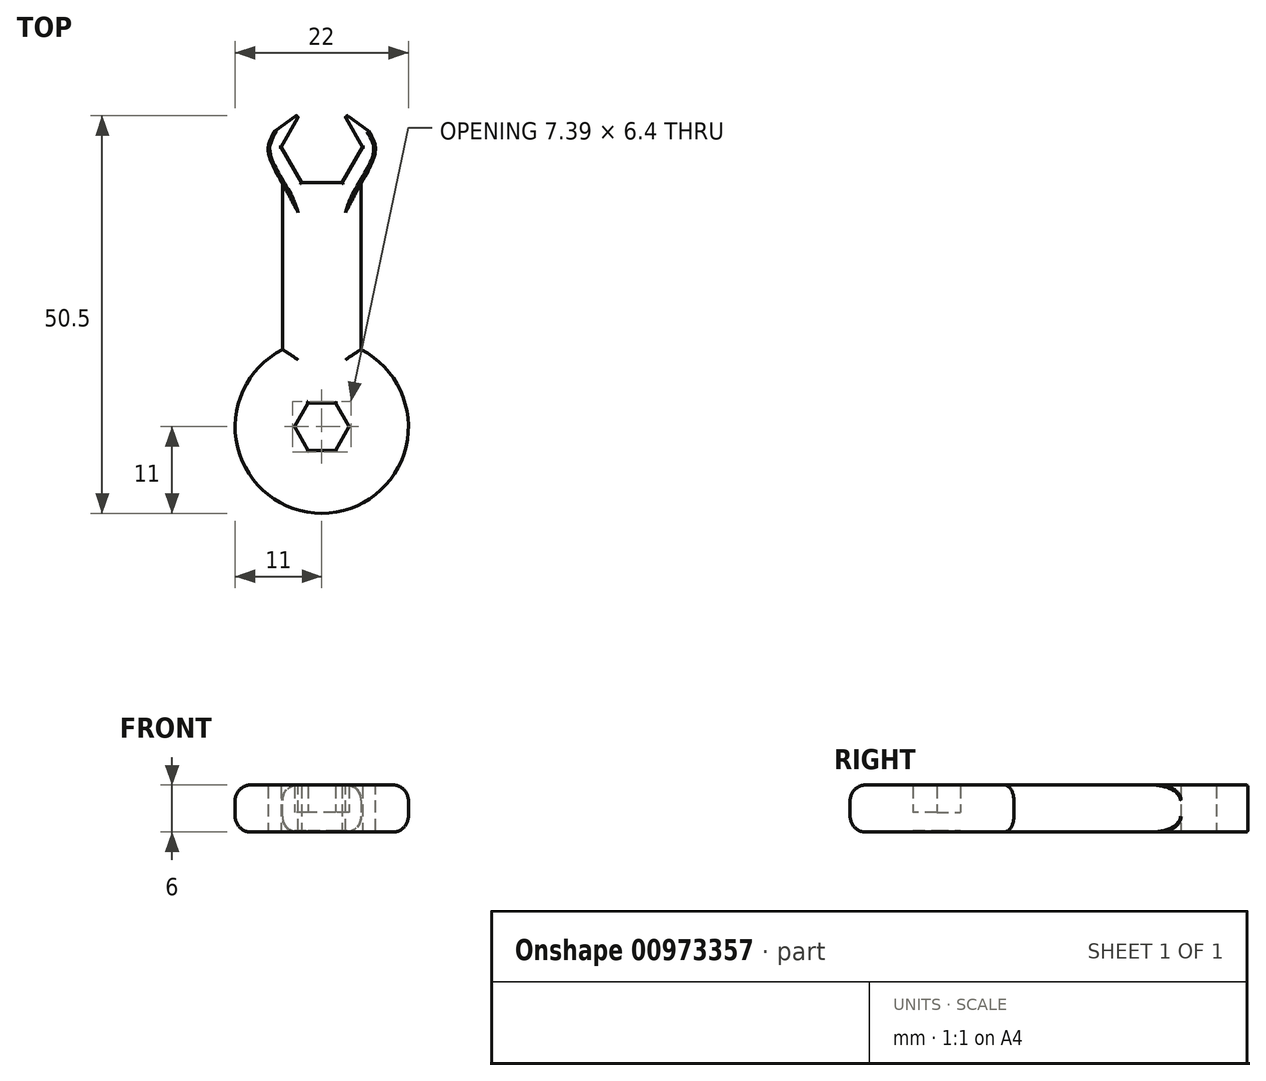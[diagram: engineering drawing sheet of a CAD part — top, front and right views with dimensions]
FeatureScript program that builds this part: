
annotation { "Feature Type Name" : "Feature", "Feature Type Description" : "" }
export const myFeature = defineFeature(function(context is Context, id is Id, definition is map)
    precondition{}
    {
        {
            var Q0;
            Q0=qCreatedBy(makeId("Top.planeOp"),FACE);
            var sketch = newSketch(context, id + "F0", { "sketchPlane" : qUnion([Q0])});
            skArc(sketch, "E0", {"start": v(-5, 9.8) * mm, "mid": v(0, -11) * mm, "end": v(5, 9.8) * mm});
            skCircle(sketch, "E1.cCircle", {"center": v(0, 0) * mm, "radius": 3 * mm, "construction": true});
            skLineSegment(sketch, "E1.0", {"start": v(1.73, -3) * mm, "end": v(-1.73, -3) * mm});
            skLineSegment(sketch, "E1.1", {"start": v(-1.73, -3) * mm, "end": v(-3.46, 0) * mm});
            skLineSegment(sketch, "E1.2", {"start": v(-3.46, 0) * mm, "end": v(-1.73, 3) * mm});
            skLineSegment(sketch, "E1.3", {"start": v(-1.73, 3) * mm, "end": v(1.73, 3) * mm});
            skLineSegment(sketch, "E1.4", {"start": v(1.73, 3) * mm, "end": v(3.46, 0) * mm});
            skLineSegment(sketch, "E1.5", {"start": v(3.46, 0) * mm, "end": v(1.73, -3) * mm});
            skPoint(sketch, "E1.0.midPoint", {"position": v(0, -3) * mm});
            skLineSegment(sketch, "E2.top", {"start": v(5, 31) * mm, "end": v(-5, 31) * mm});
            skLineSegment(sketch, "E2.left", {"start": v(5, 11) * mm, "end": v(5, 31) * mm});
            skLineSegment(sketch, "E2.right", {"start": v(-5, 11) * mm, "end": v(-5, 31) * mm});
            skLineSegment(sketch, "E3", {"start": v(5, 11) * mm, "end": v(5, 9) * mm});
            skLineSegment(sketch, "E4", {"start": v(-5, 11) * mm, "end": v(-5, 9) * mm});
            skLineSegment(sketch, "E5", {"start": v(-5, 9) * mm, "end": v(5, 9) * mm});
            skPoint(sketch, "E2.bottom.start.orphan", {"position": v(0, 11) * mm});
            skPoint(sketch, "E6.orphan", {"position": v(-8, 31) * mm});
            skPoint(sketch, "E7.startSnap0", {"position": v(0, 31) * mm});
            skPoint(sketch, "E7.end.orphan", {"position": v(0, 31) * mm});
            skPoint(sketch, "E7.start.orphan", {"position": v(0, 35.5) * mm});
            skLineSegment(sketch, "E8", {"start": v(0, 35.5) * mm, "end": v(0, 31) * mm});
            skPoint(sketch, "E9.orphan", {"position": v(2.6, 44.5) * mm});
            skPoint(sketch, "E10.5.end.orphan", {"position": v(2.6, 35.5) * mm});
            skPoint(sketch, "E10.1.start.orphan", {"position": v(-2.6, 35.5) * mm});
            skLineSegment(sketch, "E11.0", {"start": v(2.6, 31) * mm, "end": v(-2.6, 31) * mm});
            skLineSegment(sketch, "E11.1", {"start": v(-2.6, 31) * mm, "end": v(-5.2, 35.5) * mm});
            skLineSegment(sketch, "E11.5", {"start": v(5.2, 35.5) * mm, "end": v(2.6, 31) * mm});
            skPoint(sketch, "E12.orphan", {"position": v(2.6, 40) * mm});
            skPoint(sketch, "E13.start.orphan", {"position": v(-6.8, 37.68) * mm});
            skPoint(sketch, "E14.MirrorCS.end.orphan", {"position": v(5.2, 35.5) * mm});
            skPoint(sketch, "E14.MirrorCS.start.orphan", {"position": v(6.8, 37.68) * mm});
            skPoint(sketch, "E15.MirrorCS.start.orphan", {"position": v(9.24, 35.24) * mm});
            skCircle(sketch, "E16.cCircle", {"center": v(0, 35.5) * mm, "radius": 4.5 * mm, "construction": true});
            skLineSegment(sketch, "E16.3", {"start": v(-5.2, 35.5) * mm, "end": v(-2.6, 40) * mm});
            skLineSegment(sketch, "E16.5", {"start": v(2.6, 40) * mm, "end": v(5.2, 35.5) * mm});
            skPoint(sketch, "E16.0.midPoint", {"position": v(3.9, 33.25) * mm});
            skLineSegment(sketch, "E17", {"start": v(-5.92, 37.62) * mm, "end": v(-2.6, 40) * mm});
            skLineSegment(sketch, "E18", {"start": v(2.6, 40) * mm, "end": v(5.92, 37.62) * mm});
            skPoint(sketch, "E19.orphan", {"position": v(-7.81, 37.68) * mm});
            skPoint(sketch, "E20.MirrorCS.end.orphan", {"position": v(7.81, 37.68) * mm});
            skPoint(sketch, "E21.end.orphan", {"position": v(-5.92, 37.62) * mm});
            skFitSpline(sketch, "E22", {"points": [v(-5, 31) * mm, v(-6.8, 35.24) * mm, v(-5.92, 37.62) * mm], "startDerivative": vector(-4.66, 7.9) * mm, "endDerivative": vector(3.2, 5.2) * mm});
            skPoint(sketch, "E23.orphan", {"position": v(-9.24, 35.24) * mm});
            skFitSpline(sketch, "E24.MirrorCS", {"points": [v(5, 31) * mm, v(6.8, 35.24) * mm, v(5.92, 37.62) * mm], "startDerivative": vector(4.66, 7.9) * mm, "endDerivative": vector(-3.2, 5.2) * mm});
            skSolve(sketch);
        }
        {
            var Q0;
            {var subQ1=sQuery(id+"F0.wireOp",EDGE,"E0");Q0=makeQuery(id+"F0.imprint","IMPRINT",FACE,{"disambiguationData":[TD([[makeQuery(id+"F0.imprint","IMPRINT",EDGE,{"derivedFrom":subQ1}),1.0]])]});}
            var Q1;
            {var subQ7=sQuery(id+"F0.wireOp",EDGE,"E2.left");Q1=makeQuery(id+"F0.imprint","IMPRINT",FACE,{"disambiguationData":[TD([[makeQuery(id+"F0.imprint","IMPRINT",EDGE,{"derivedFrom":subQ7}),1.0]])]});}
            var Q2;
            {var subQ0=sQuery(id+"F0.wireOp",EDGE,"E11.1");Q2=makeQuery(id+"F0.imprint","IMPRINT",FACE,{"disambiguationData":[TD([[makeQuery(id+"F0.imprint","IMPRINT",EDGE,{"derivedFrom":subQ0}),1.0]])]});}
            var Q3;
            {var subQ0=sQuery(id+"F0.wireOp",EDGE,"E11.5");Q3=makeQuery(id+"F0.imprint","IMPRINT",FACE,{"disambiguationData":[TD([[makeQuery(id+"F0.imprint","IMPRINT",EDGE,{"derivedFrom":subQ0}),1.0]])]});}
            extrude(context, id + "F1", {"entities" : qUnion([Q0, Q1, Q2, Q3]), "depth" : 6 * mm, "offsetDistance" : 25 * mm});
        }
        {
            var Q0;
            Q0=makeQuery(id+"F1.opExtrude","SWEPT_EDGE",EDGE,{"disambiguationData":[OSD([sQuery(id+"F0.wireOp",EDGE,"KDg4HD6V-isxW-cNXE-fjSG-ZOqcz2IWWXIc"),sQuery(id+"F0.wireOp",EDGE,"Dl8Gz6KM-Olm8-RAhG-Kqo9-J7DI2SJ82FjE")])]});
            var Q1;
            Q1=makeQuery(id+"F1.opExtrude","SWEPT_EDGE",EDGE,{"disambiguationData":[OSD([sQuery(id+"F0.wireOp",EDGE,"7af5c376-e6ad-482c-982b-24b6638f54230.MirrorCS"),sQuery(id+"F0.wireOp",EDGE,"E20.MirrorCS")])]});
            var Q2;
            Q2=makeQuery(id+"F1.opExtrude","CAP_EDGE",EDGE,{"disambiguationData":[OSD([sQuery(id+"F0.wireOp",EDGE,"E2.left"),sQuery(id+"F0.wireOp",EDGE,"E3")])],"isStart":false});
            var Q3;
            Q3=makeQuery(id+"F1.opExtrude","CAP_EDGE",EDGE,{"disambiguationData":[OSD([sQuery(id+"F0.wireOp",EDGE,"E2.right"),sQuery(id+"F0.wireOp",EDGE,"E4")])],"isStart":false});
            var Q4;
            Q4=makeQuery(id+"F1.opExtrude","CAP_EDGE",EDGE,{"disambiguationData":[OSD([sQuery(id+"F0.wireOp",EDGE,"E2.right"),sQuery(id+"F0.wireOp",EDGE,"E4")])],"isStart":true});
            var Q5;
            Q5=makeQuery(id+"F1.opExtrude","CAP_EDGE",EDGE,{"disambiguationData":[OSD([sQuery(id+"F0.wireOp",EDGE,"E2.left"),sQuery(id+"F0.wireOp",EDGE,"E3")])],"isStart":true});
            var Q6;
            Q6=makeQuery(id+"F1.opExtrude","CAP_EDGE",EDGE,{"disambiguationData":[OSD([sQuery(id+"F0.wireOp",EDGE,"E0")])],"isStart":true});
            var Q7;
            Q7=makeQuery(id+"F1.opExtrude","CAP_EDGE",EDGE,{"disambiguationData":[OSD([sQuery(id+"F0.wireOp",EDGE,"E0")])],"isStart":false});
            fillet(context, id + "F2", {"entities" : qUnion([Q0, Q1, Q2, Q3, Q4, Q5, Q6, Q7]), "tangentPropagation" : true, "radius" : 2 * mm, "defaultsChanged" : false, "vertexSettings" : [], "allowEdgeOverflow" : false});
        }
        {
            var Q0;
            Q0=makeQuery(id+"F1.opExtrude","SWEPT_FACE",FACE,{"disambiguationData":[OSD([sQuery(id+"F0.wireOp",EDGE,"E18")])]});
            var Q1;
            Q1=makeQuery(id+"F1.opExtrude","SWEPT_FACE",FACE,{"disambiguationData":[OSD([sQuery(id+"F0.wireOp",EDGE,"E24.MirrorCS")])]});
            var Q2;
            Q2=makeQuery(id+"F1.opExtrude","CAP_FACE",FACE,{"disambiguationData":[OSD([sQuery(id+"F0.wireOp",EDGE,"E0"),sQuery(id+"F0.wireOp",EDGE,"E1.0"),sQuery(id+"F0.wireOp",EDGE,"E1.1"),sQuery(id+"F0.wireOp",EDGE,"E1.2"),sQuery(id+"F0.wireOp",EDGE,"E1.3"),sQuery(id+"F0.wireOp",EDGE,"E1.4"),sQuery(id+"F0.wireOp",EDGE,"E1.5"),sQuery(id+"F0.wireOp",EDGE,"E2.top"),sQuery(id+"F0.wireOp",EDGE,"E2.left"),sQuery(id+"F0.wireOp",EDGE,"E2.right"),sQuery(id+"F0.wireOp",EDGE,"E3"),sQuery(id+"F0.wireOp",EDGE,"E4"),sQuery(id+"F0.wireOp",EDGE,"E11.1"),sQuery(id+"F0.wireOp",EDGE,"E11.5"),sQuery(id+"F0.wireOp",EDGE,"E16.3"),sQuery(id+"F0.wireOp",EDGE,"E16.5"),sQuery(id+"F0.wireOp",EDGE,"E17"),sQuery(id+"F0.wireOp",EDGE,"E18"),sQuery(id+"F0.wireOp",EDGE,"E22"),sQuery(id+"F0.wireOp",EDGE,"E24.MirrorCS")])],"isStart":true});
            var Q3;
            Q3=makeQuery(id+"F1.opExtrude","SWEPT_FACE",FACE,{"disambiguationData":[OSD([sQuery(id+"F0.wireOp",EDGE,"E22")])]});
            var Q4;
            Q4=makeQuery(id+"F1.opExtrude","SWEPT_FACE",FACE,{"disambiguationData":[OSD([sQuery(id+"F0.wireOp",EDGE,"E17")])]});
            var Q5;
            Q5=makeQuery(id+"F1.opExtrude","CAP_FACE",FACE,{"disambiguationData":[OSD([sQuery(id+"F0.wireOp",EDGE,"E0"),sQuery(id+"F0.wireOp",EDGE,"E1.0"),sQuery(id+"F0.wireOp",EDGE,"E1.1"),sQuery(id+"F0.wireOp",EDGE,"E1.2"),sQuery(id+"F0.wireOp",EDGE,"E1.3"),sQuery(id+"F0.wireOp",EDGE,"E1.4"),sQuery(id+"F0.wireOp",EDGE,"E1.5"),sQuery(id+"F0.wireOp",EDGE,"E2.top"),sQuery(id+"F0.wireOp",EDGE,"E2.left"),sQuery(id+"F0.wireOp",EDGE,"E2.right"),sQuery(id+"F0.wireOp",EDGE,"E3"),sQuery(id+"F0.wireOp",EDGE,"E4"),sQuery(id+"F0.wireOp",EDGE,"E11.1"),sQuery(id+"F0.wireOp",EDGE,"E11.5"),sQuery(id+"F0.wireOp",EDGE,"E16.3"),sQuery(id+"F0.wireOp",EDGE,"E16.5"),sQuery(id+"F0.wireOp",EDGE,"E17"),sQuery(id+"F0.wireOp",EDGE,"E18"),sQuery(id+"F0.wireOp",EDGE,"E22"),sQuery(id+"F0.wireOp",EDGE,"E24.MirrorCS")])],"isStart":false});
            fillet(context, id + "F3", {"entities" : qUnion([Q0, Q1, Q2, Q3, Q4, Q5]), "tangentPropagation" : true, "radius" : 0.2 * mm, "defaultsChanged" : false, "vertexSettings" : [], "allowEdgeOverflow" : false});
        }
        {
            var Q0;
            Q0=makeQuery(id+"F0.imprint","IMPRINT",FACE,{"disambiguationData":[TD([[makeQuery(id+"F0.imprint","IMPRINT",EDGE,{"derivedFrom":sQuery(id+"F0.wireOp",EDGE,"E1.0")}),-1.0]])]});
            extrude(context, id + "F4", {"entities" : qUnion([Q0]), "operationType" : NewBodyOperationType.ADD, "depth" : 2.5 * mm, "offsetDistance" : 25 * mm});
        }
    });
